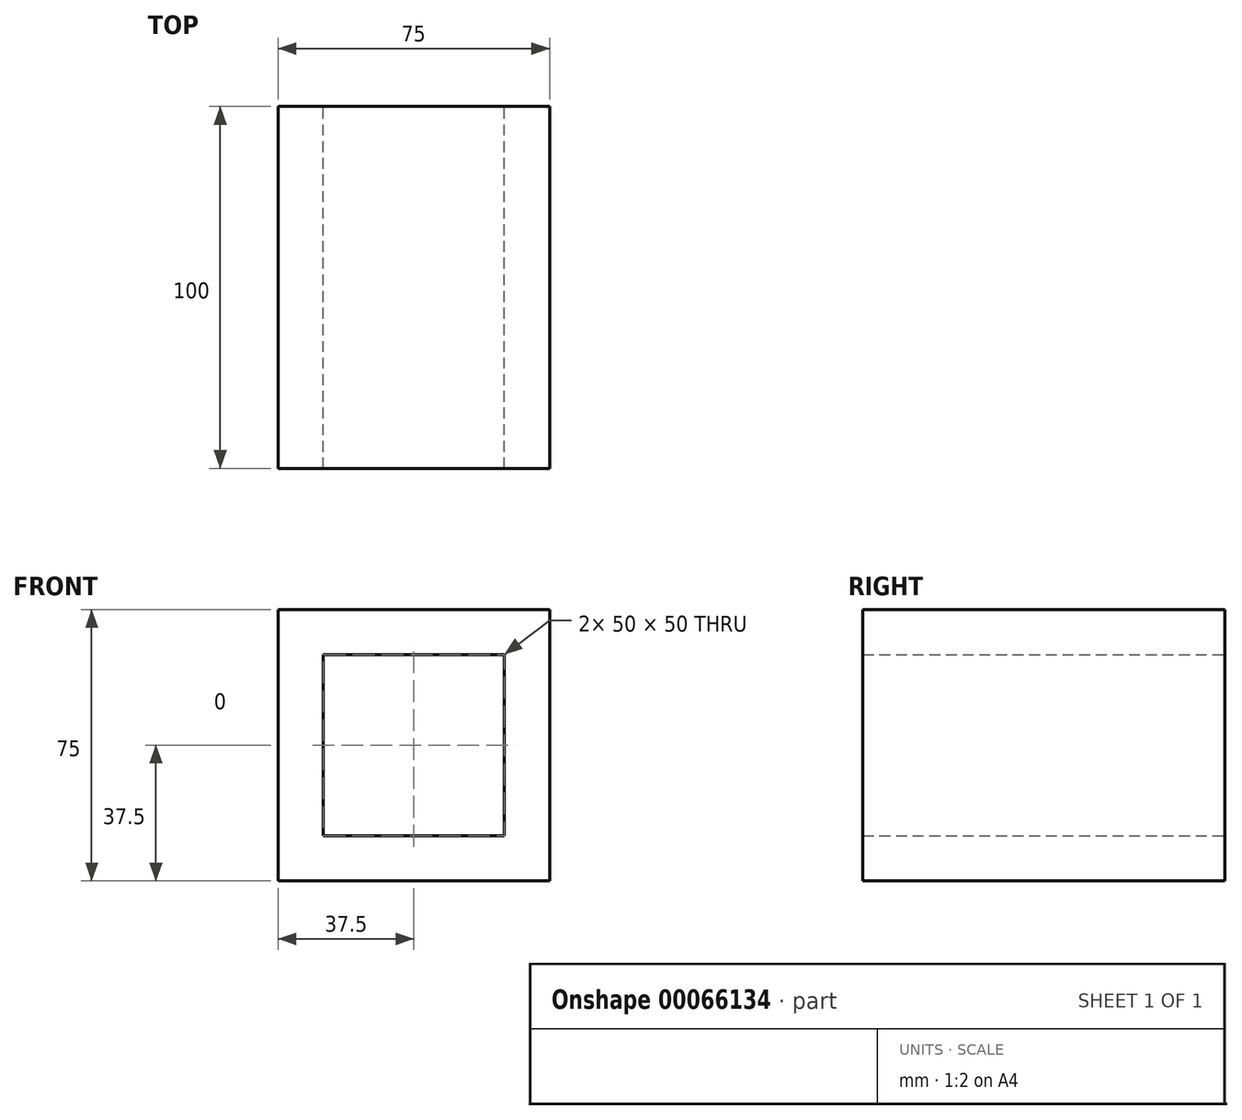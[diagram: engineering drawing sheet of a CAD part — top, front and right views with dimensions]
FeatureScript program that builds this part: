
annotation { "Feature Type Name" : "Feature", "Feature Type Description" : "" }
export const myFeature = defineFeature(function(context is Context, id is Id, definition is map)
    precondition{}
    {
        {
            var Q0;
            Q0=qCreatedBy(makeId("Front.planeOp"),FACE);
            var sketch = newSketch(context, id + "F0", { "sketchPlane" : qUnion([Q0])});
            skLineSegment(sketch, "E0.rect.bottom", {"start": v(25, -25) * mm, "end": v(-25, -25) * mm});
            skLineSegment(sketch, "E0.rect.top", {"start": v(25, 25) * mm, "end": v(-25, 25) * mm});
            skLineSegment(sketch, "E0.rect.left", {"start": v(25, -25) * mm, "end": v(25, 25) * mm});
            skLineSegment(sketch, "E0.rect.right", {"start": v(-25, -25) * mm, "end": v(-25, 25) * mm});
            skPoint(sketch, "E0.rect.middle", {"position": v(0, 0) * mm});
            skLineSegment(sketch, "E1.rect.bottom", {"start": v(37.5, 37.5) * mm, "end": v(-37.5, 37.5) * mm});
            skLineSegment(sketch, "E1.rect.top", {"start": v(37.5, -37.5) * mm, "end": v(-37.5, -37.5) * mm});
            skLineSegment(sketch, "E1.rect.left", {"start": v(37.5, 37.5) * mm, "end": v(37.5, -37.5) * mm});
            skLineSegment(sketch, "E1.rect.right", {"start": v(-37.5, 37.5) * mm, "end": v(-37.5, -37.5) * mm});
            skSolve(sketch);
        }
        {
            var Q0;
            Q0 = qSketchRegion(id + "F0", true);
            extrude(context, id + "F1", {"entities" : qUnion([Q0]), "depth" : 100 * mm});
        }
    });
